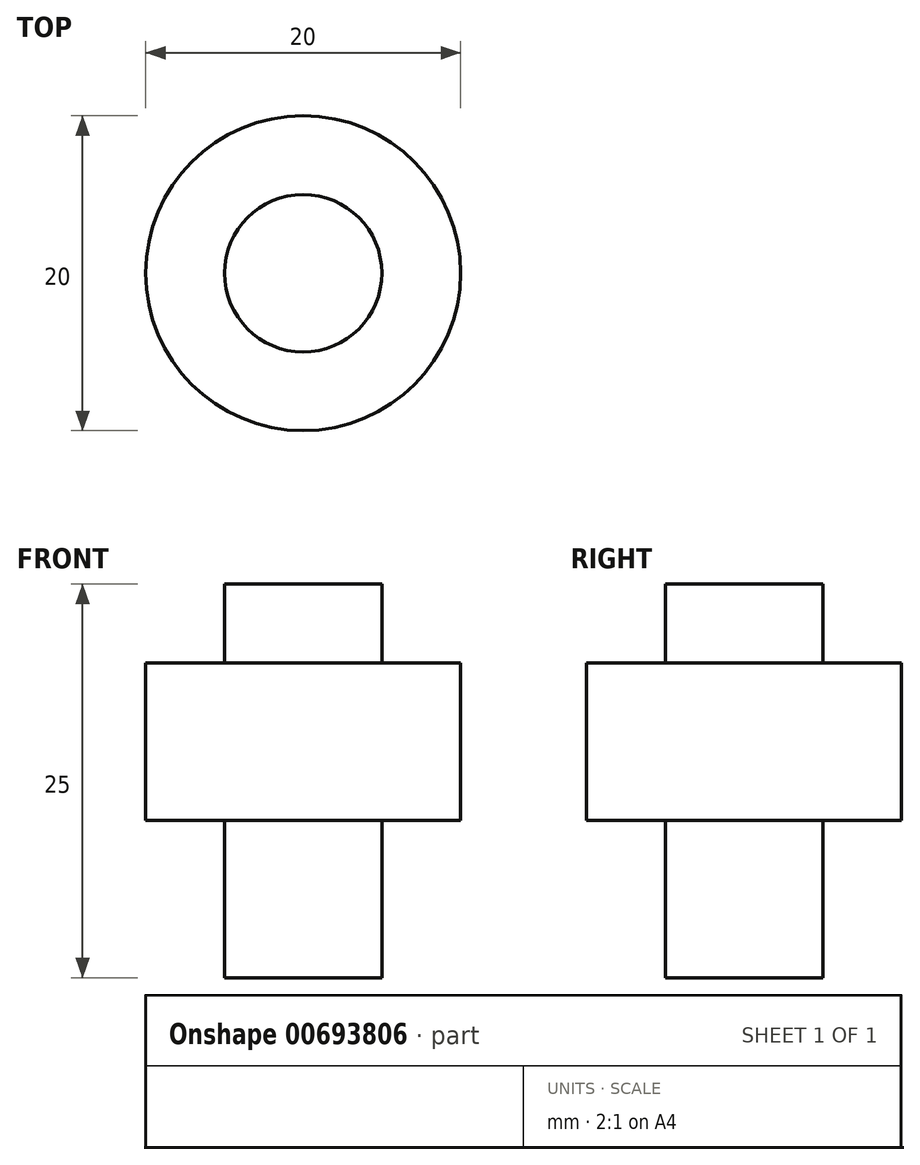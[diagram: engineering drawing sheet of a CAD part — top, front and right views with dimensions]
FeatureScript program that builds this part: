
annotation { "Feature Type Name" : "Feature", "Feature Type Description" : "" }
export const myFeature = defineFeature(function(context is Context, id is Id, definition is map)
    precondition{}
    {
        {
            var Q0;
            Q0=qCreatedBy(makeId("Top.planeOp"),FACE);
            var sketch = newSketch(context, id + "F0", { "sketchPlane" : qUnion([Q0])});
            skCircle(sketch, "E0", {"center": v(0, 0) * mm, "radius": 10 * mm});
            skSolve(sketch);
        }
        {
            var Q0;
            Q0 = qSketchRegion(id + "F0", true);
            extrude(context, id + "F1", {"entities" : qUnion([Q0]), "depth" : 10 * mm, "offsetDistance" : 25 * mm});
        }
        {
            var Q0;
            Q0=qCreatedBy(makeId("Top.planeOp"),FACE);
            var sketch = newSketch(context, id + "F2", { "sketchPlane" : qUnion([Q0])});
            skCircle(sketch, "E1", {"center": v(0, 0) * mm, "radius": 5 * mm});
            skSolve(sketch);
        }
        {
            var Q0;
            Q0 = qSketchRegion(id + "F2", true);
            extrude(context, id + "F3", {"entities" : qUnion([Q0]), "operationType" : NewBodyOperationType.ADD, "depth" : 15 * mm, "offsetDistance" : 25 * mm});
        }
        {
            var Q0;
            Q0 = qSketchRegion(id + "F2", true);
            extrude(context, id + "F4", {"entities" : qUnion([Q0]), "operationType" : NewBodyOperationType.ADD, "oppositeDirection" : true, "depth" : 10 * mm, "offsetDistance" : 25 * mm});
        }
    });
